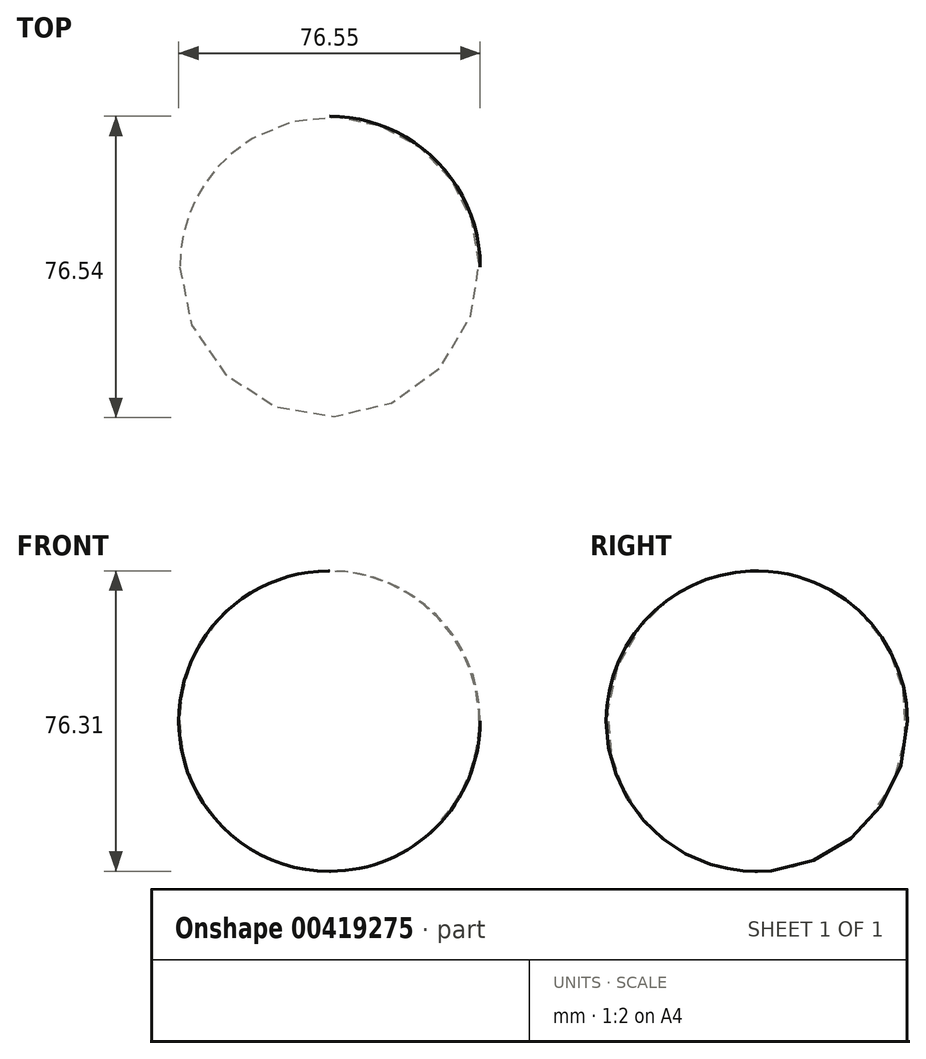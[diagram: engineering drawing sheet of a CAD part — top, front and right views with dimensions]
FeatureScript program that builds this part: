
annotation { "Feature Type Name" : "Feature", "Feature Type Description" : "" }
export const myFeature = defineFeature(function(context is Context, id is Id, definition is map)
    precondition{}
    {
        {
            var Q0;
            Q0=qCreatedBy(makeId("Front.planeOp"),FACE);
            var sketch = newSketch(context, id + "F0", { "sketchPlane" : qUnion([Q0])});
            skArc(sketch, "E0", {"start": v(0.02, 38.15) * mm, "mid": v(-38.15, -0.1) * mm, "end": v(0.22, -38.15) * mm});
            skLineSegment(sketch, "E1", {"start": v(0.02, 38.15) * mm, "end": v(0.22, -38.15) * mm});
            skSolve(sketch);
        }
        {
            var Q0;
            Q0 = qSketchRegion(id + "F0", true);
            var Q1;
            Q1=sQuery(id+"F0.wireOp",EDGE,"E1");
            revolve(context, id + "F1", {"entities" : qUnion([Q0]), "axis" : qUnion([Q1]), "revolveType" : RevolveType.FULL});
        }
    });
